# Revit family: НЕВАТОМ_Гибкая вставка AxB, Версия 1
name_source: partatom
category: Обобщенные модели
revit_build: Autodesk Revit 2017 (Build: 20170118_1100(x64)
units: mm (PartAtom-declared; Revit-internal decimal feet)

## family parameters
Всегда вертикально = Да
Может служить основой для арматурных стержней = Нет
На основе рабочей плоскости = Нет
Общий = Нет
При загрузке вырезать с полостями = Нет
Размер круглого соединителя = Использовать диаметр
Тип детали = Нормальный
Точка расчета площади = Нет

## types (1)
- НЕВАТОМ_Гибкая вставка AxB, Версия 1
    A = 180 мм
    A1 = 155 мм
    ADSK_Единица измерения = шт.
    ADSK_Завод-изготовитель = НЕВАТОМ
    ADSK_Марка = Гибкая вставка ВГ 180x180
    ADSK_Масса = 1.786
    ADSK_Материал наименование = Сталь
    ADSK_Наименование = Гибкая вставка ВГ 180x180
    B = 180 мм
    B2 = 155 мм
    L = 60 мм
    L1 = 56 мм
    Type = 180 мм
    a = 160 мм
    b = 160 мм
    t = 2 мм
    t1 = 54 мм
    Вставка ВГ = НЕВАТОМ_Гибкая вставка VR_пр, Версия 1
    Материал = Сталь
